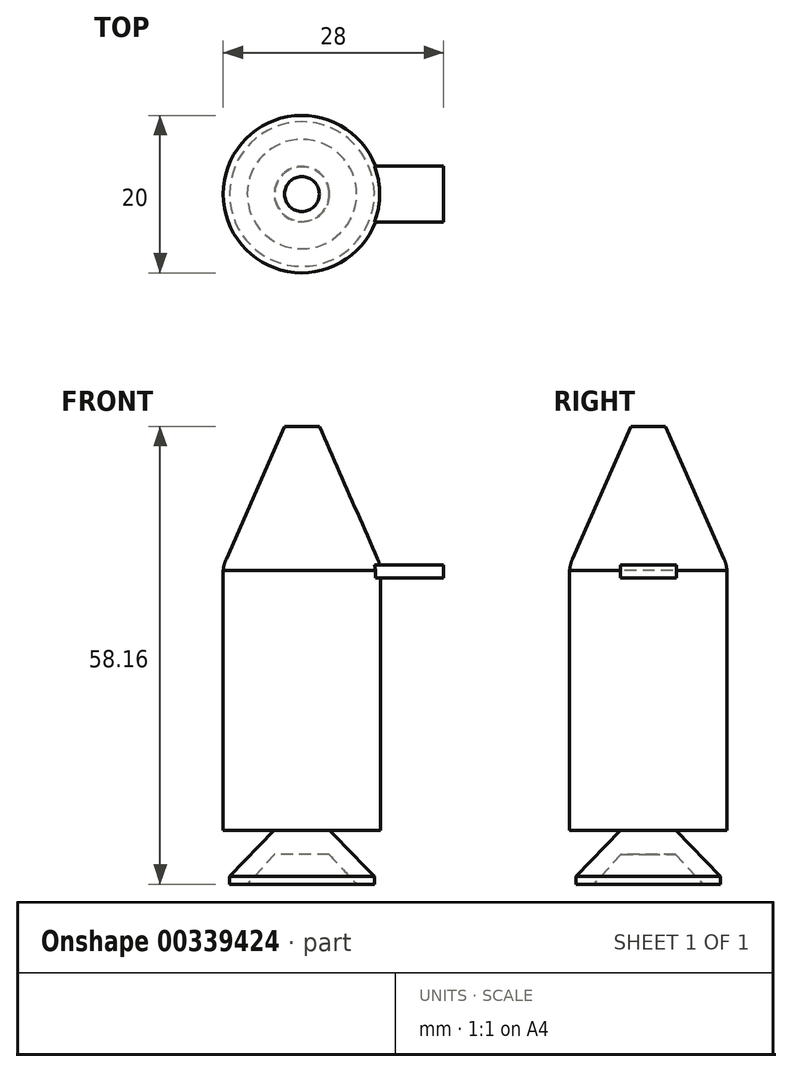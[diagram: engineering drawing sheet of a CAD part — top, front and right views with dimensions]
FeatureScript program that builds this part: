
annotation { "Feature Type Name" : "Feature", "Feature Type Description" : "" }
export const myFeature = defineFeature(function(context is Context, id is Id, definition is map)
    precondition{}
    {
        {
            var Q0;
            Q0=qCreatedBy(makeId("Front.planeOp"),FACE);
            var sketch = newSketch(context, id + "F0", { "sketchPlane" : qUnion([Q0])});
            skLineSegment(sketch, "E0", {"start": v(0, 30.9) * mm, "end": v(0, -23.48) * mm, "construction": true});
            skLineSegment(sketch, "E1", {"start": v(-2.2, 30.9) * mm, "end": v(-9.6, 14.09) * mm});
            skLineSegment(sketch, "E2", {"start": v(-10, 12.62) * mm, "end": v(-10, -20.43) * mm});
            skLineSegment(sketch, "E3", {"start": v(-10, -20.43) * mm, "end": v(-3.52, -20.43) * mm});
            skLineSegment(sketch, "E4", {"start": v(-3.52, -20.43) * mm, "end": v(-9.2, -26.3) * mm});
            skLineSegment(sketch, "E5", {"start": v(-9.2, -26.3) * mm, "end": v(-9.2, -27.25) * mm});
            skLineSegment(sketch, "E6", {"start": v(-9.2, -27.25) * mm, "end": v(-6.95, -27.25) * mm});
            skLineSegment(sketch, "E7", {"start": v(0, -27.25) * mm, "end": v(0, 35.92) * mm});
            skPoint(sketch, "E8.visualSharp", {"position": v(-9.57, 14.16) * mm});
            skArc(sketch, "E8.filletArc", {"start": v(-9.6, 14.09) * mm, "mid": v(-9.86, 13.37) * mm, "end": v(-10, 12.62) * mm});
            skLineSegment(sketch, "E9", {"start": v(-6.95, -27.25) * mm, "end": v(-3.46, -23.48) * mm});
            skLineSegment(sketch, "E10", {"start": v(-3.46, -23.48) * mm, "end": v(0, -23.48) * mm});
            skLineSegment(sketch, "E11.trimOffspring", {"start": v(0, -25) * mm, "end": v(0, -27.25) * mm, "construction": true});
            skLineSegment(sketch, "E12", {"start": v(0, 30.9) * mm, "end": v(-2.2, 30.9) * mm});
            skSolve(sketch);
        }
        {
            var Q0;
            Q0=makeQuery(id+"F0.imprint","IMPRINT",FACE,{"disambiguationData":[TD([[makeQuery(id+"F0.imprint","IMPRINT",EDGE,{"derivedFrom":sQuery(id+"F0.wireOp",EDGE,"E1")}),1.0]])]});
            var Q1;
            Q1=sQuery(id+"F0.wireOp",EDGE,"E0");
            revolve(context, id + "F1", {"entities" : qUnion([Q0]), "axis" : qUnion([Q1]), "revolveType" : RevolveType.FULL});
        }
        {
            var Q0;
            Q0=qCreatedBy(makeId("Right.planeOp"),FACE);
            var sketch = newSketch(context, id + "F2", { "sketchPlane" : qUnion([Q0])});
            skLineSegment(sketch, "E13.bottom", {"start": v(3.56, 11.64) * mm, "end": v(-3.56, 11.64) * mm});
            skLineSegment(sketch, "E13.top", {"start": v(3.56, 13.3) * mm, "end": v(-3.56, 13.3) * mm});
            skLineSegment(sketch, "E13.left", {"start": v(3.56, 11.64) * mm, "end": v(3.56, 13.3) * mm});
            skLineSegment(sketch, "E13.right", {"start": v(-3.56, 11.64) * mm, "end": v(-3.56, 13.3) * mm});
            skPoint(sketch, "E13.middle", {"position": v(0, 12.47) * mm});
            skSolve(sketch);
        }
        {
            var Q0;
            Q0 = qSketchRegion(id + "F2", true);
            extrude(context, id + "F3", {"entities" : qUnion([Q0]), "operationType" : NewBodyOperationType.ADD, "depth" : 18 * mm});
        }
    });
